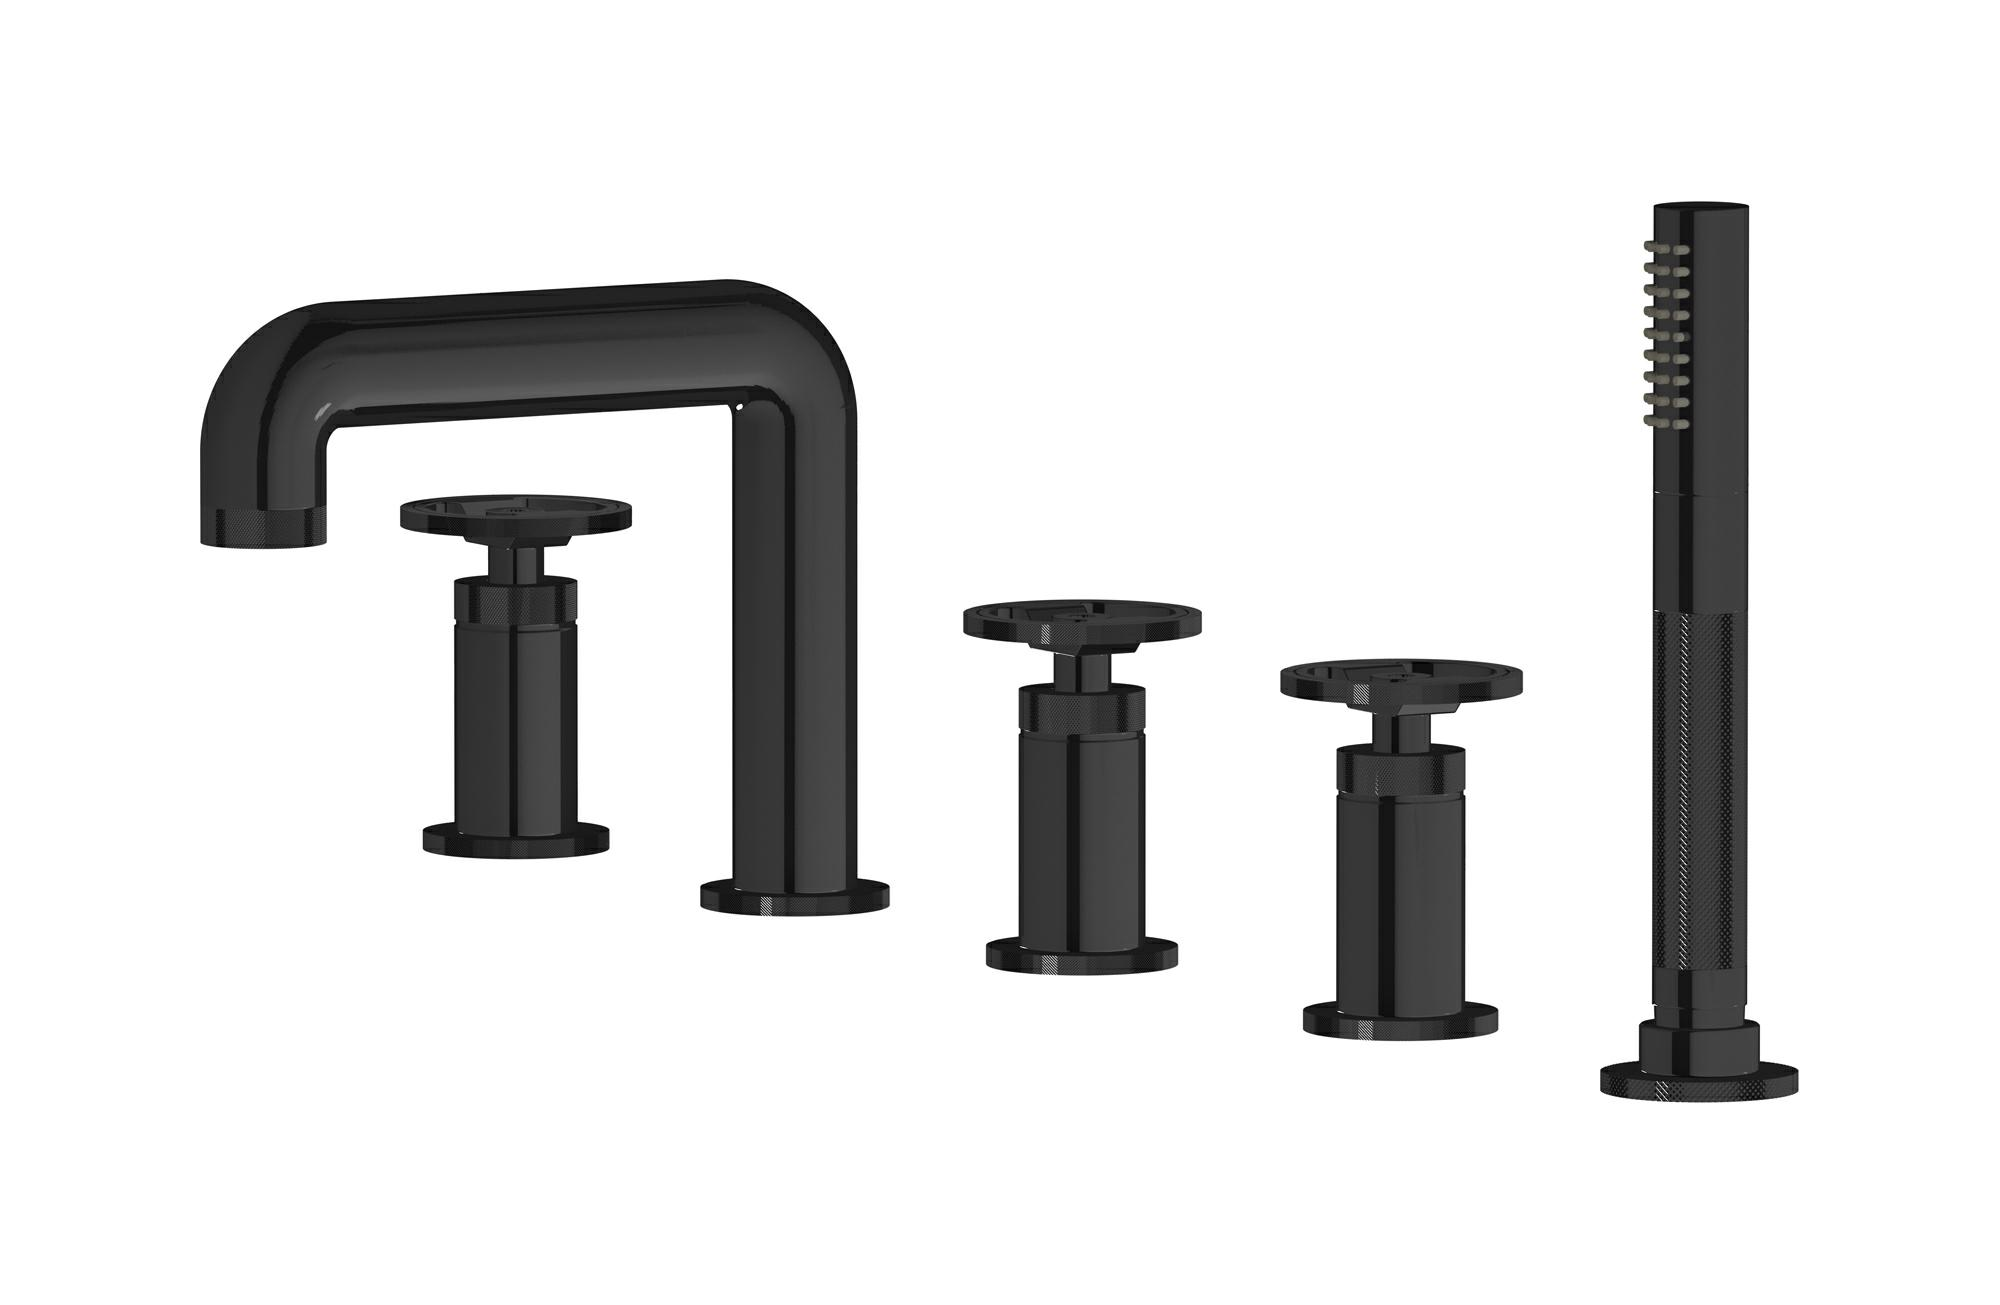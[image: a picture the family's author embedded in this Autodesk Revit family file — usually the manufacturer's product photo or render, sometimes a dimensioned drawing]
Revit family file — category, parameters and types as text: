
# Revit family: B1396
name_source: partatom
category: Apparecchi idraulici
units: mm (PartAtom-declared; Revit-internal decimal feet)

## family parameters
Basato su piano di lavoro = No
Condiviso = No
Mantieni orientamento annotazione = No
Numero OmniClass = 23.45.55.17
Punto di calcolo locali = No
Quota connettore circolare = Usa diametro
Sempre verticale = Sì
Taglio con vuoti quando caricato = No
Tipo di parte = Normale
Titolo OmniClass = Mixing Faucets

## types (13) — shared parameters
Cold water inlet = 10 mm  [stored 0.0328084 ft]
Commenti sul tipo = Five holes deck mounted bath filler with shower kit
Connessione CW = No
Connessione HW = No
Connessione di scarico = No
Connessione di ventilazione = No
Descrizione = Five holes deck mounted bath filler with shower kit
Hot water inlet = 10 mm  [stored 0.0328084 ft]
Produttore = IB Rubinetterie S.p.A.
URL = https://www.weareib.it
zero-valued in all types: Prospetto di default

## per-type parameters (varying)
| type | Finishes surface | Immagine tipo | Modello |
| Chrome | IB_Chrome | B1396CC.jpg | B1396CC |
| Black Chrome | IB_Black chrome | B1396CF.jpg | B1396CF |
| Brushed Black Chrome | IB_Brushed black chrome | B1396CS.jpg | B1396CS |
| Pale Gold | IB_Pale gold | B1396II.jpg | B1396II |
| Brushed Pale Gold | IB_brushed pale gold | B1396IS.jpg | B1396IS |
| Matt Black | IB_matt black | B1396NP.jpg | B1396NP |
| Natural Brass | IB_Brass | B1396ON.jpg | B1396ON |
| Gold | IB_gold | B1396OO.jpg | B1396OO |
| Brushed Gold | IB_brushed gold | B1396OS.jpg | B1396OS |
| Rose Gold | IB_Rose gold | B1396RS.jpg | B1396RS |
| Brushed Rose Gold | IB_Brushed rose gold | B1396SR.jpg | B1396SR |
| Brushed Nickel | IB_Brushed nickel | B1396SS.jpg | B1396SS |
| Modern Bronze | IB_Modern bronze | B1396MB.jpg | B1396MB |

note: [stored X ft] marks values corroborated as IEEE doubles in the binary element streams (Revit-internal decimal feet)
